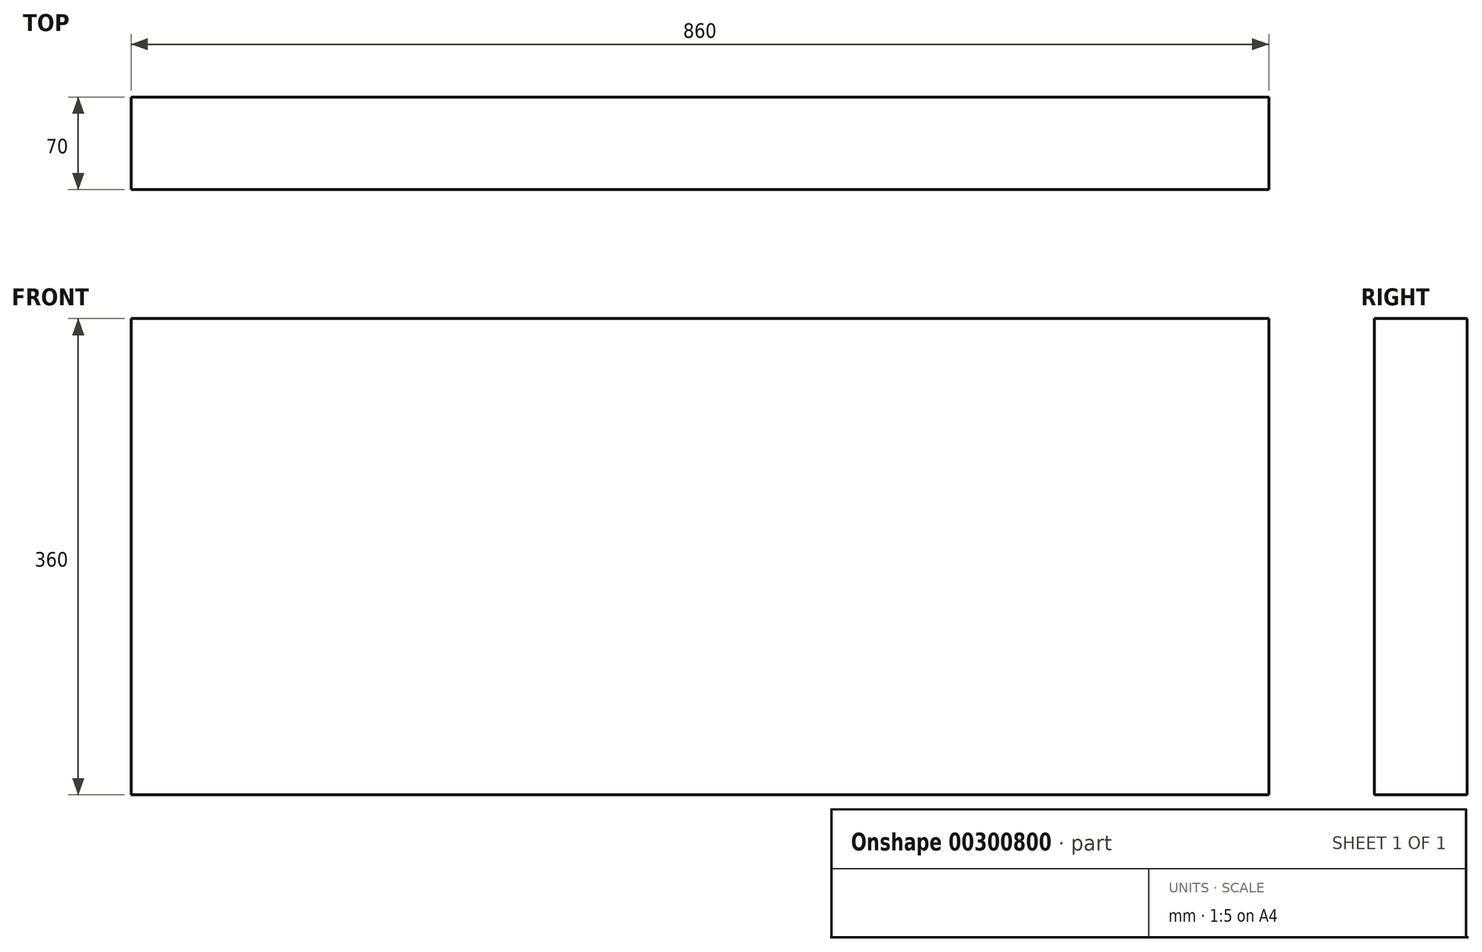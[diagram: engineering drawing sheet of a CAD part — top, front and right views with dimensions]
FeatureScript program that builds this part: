
annotation { "Feature Type Name" : "Feature", "Feature Type Description" : "" }
export const myFeature = defineFeature(function(context is Context, id is Id, definition is map)
    precondition{}
    {
        {
            var Q0;
            Q0=qCreatedBy(makeId("Front.planeOp"),FACE);
            var sketch = newSketch(context, id + "F0", { "sketchPlane" : qUnion([Q0])});
            skLineSegment(sketch, "E0.bottom", {"start": v(0, 0) * mm, "end": v(860, 0) * mm});
            skLineSegment(sketch, "E0.top", {"start": v(0, -360) * mm, "end": v(860, -360) * mm});
            skLineSegment(sketch, "E0.left", {"start": v(0, 0) * mm, "end": v(0, -360) * mm});
            skLineSegment(sketch, "E0.right", {"start": v(860, 0) * mm, "end": v(860, -360) * mm});
            skSolve(sketch);
        }
        {
            var Q0;
            Q0=makeQuery(id+"F0.imprint","IMPRINT",FACE,{"disambiguationData":[TD([[makeQuery(id+"F0.imprint","IMPRINT",EDGE,{"derivedFrom":sQuery(id+"F0.wireOp",EDGE,"E0.bottom")}),-1.0]])]});
            extrude(context, id + "F1", {"entities" : qUnion([Q0]), "depth" : 70 * mm});
        }
    });
